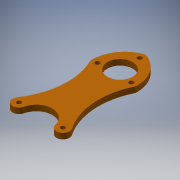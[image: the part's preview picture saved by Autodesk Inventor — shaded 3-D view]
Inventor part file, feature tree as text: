
AUTODESK INVENTOR PART (.ipt)
format: ipt  version: 2017 SP1 (Build 210196100, 196)  size: 153,088 bytes
history: native  units: in
note: dims shown in document units (in); Inventor stores cm internally (conversion verified against a paired STEP export)
features: extrude x1, sketch x1
ambient origin geometry x8: Origin, YZ Plane, XZ Plane, XY Plane, X Axis, Y Axis, Z Axis, Center Point
bodies: Solid1 (feature_tree)
feature tree (2):
  extrude  "Extrusion1"  Depth=0.25in
  sketch  "Sketch1"  dims[d0=1.125in d1=0.625in d3=0.196in d4=3.501in d5=4.0in d7=2.0in d8=0.2in d9=0.375in d10=1.5in d12=0.25in d15=0.25in d16=0.0in d18=1.125in d19=0.375in d20=60.0deg d23=1.375in d25=0.1875in d26=1.375in d27=1.0in]
